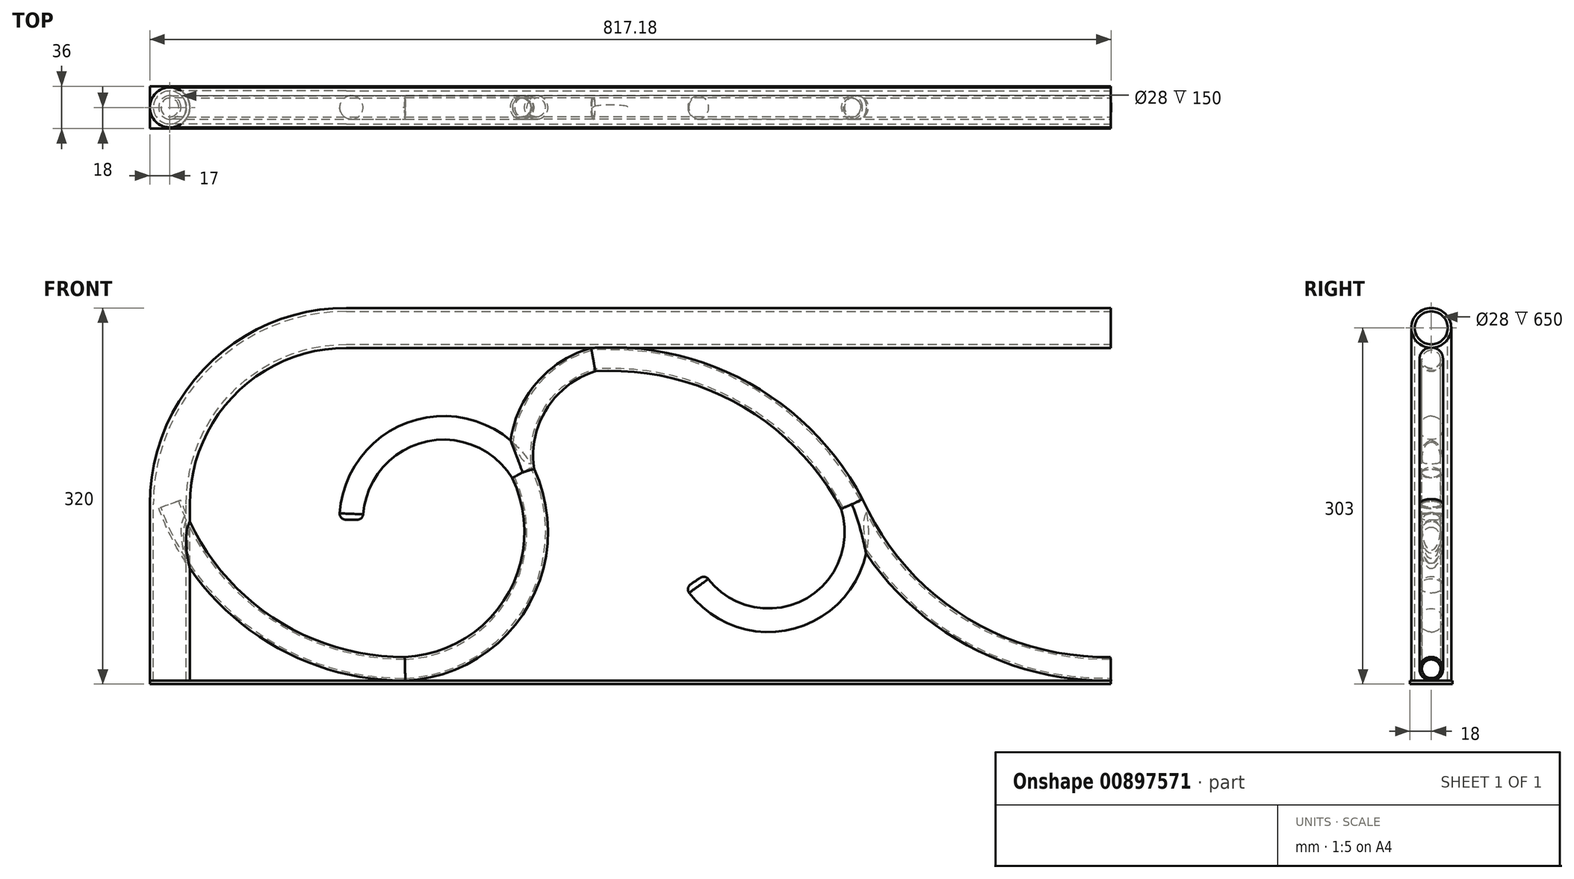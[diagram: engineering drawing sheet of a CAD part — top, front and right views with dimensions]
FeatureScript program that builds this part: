
annotation { "Feature Type Name" : "Feature", "Feature Type Description" : "" }
export const myFeature = defineFeature(function(context is Context, id is Id, definition is map)
    precondition{}
    {
        {
            var Q0;
            Q0=qCreatedBy(makeId("Front.planeOp"),FACE);
            var sketch = newSketch(context, id + "F0", { "sketchPlane" : qUnion([Q0])});
            skLineSegment(sketch, "E0", {"start": v(-800, 150) * mm, "end": v(-800, 0) * mm});
            skLineSegment(sketch, "E1", {"start": v(-800, 0) * mm, "end": v(0, 0) * mm});
            skLineSegment(sketch, "E2", {"start": v(0, 0) * mm, "end": v(0, 300) * mm});
            skLineSegment(sketch, "E3", {"start": v(-650, 300) * mm, "end": v(0, 300) * mm});
            skArc(sketch, "E4", {"start": v(-800, 150) * mm, "mid": v(-722.2, 48.28) * mm, "end": v(-600, 10) * mm});
            skLineSegment(sketch, "E5", {"start": v(-600, 10) * mm, "end": v(-600, 300) * mm, "construction": true});
            skLineSegment(sketch, "E6", {"start": v(-600, 177.08) * mm, "end": v(-500, 177.08) * mm, "construction": true});
            skArc(sketch, "E7", {"start": v(-600, 10) * mm, "mid": v(-505.06, 66.64) * mm, "end": v(-500, 177.08) * mm});
            skArc(sketch, "E8", {"start": v(-440, 273) * mm, "mid": v(-488.19, 236.41) * mm, "end": v(-500, 177.08) * mm});
            skLineSegment(sketch, "E9", {"start": v(0, 150) * mm, "end": v(-220, 150) * mm, "construction": true});
            skArc(sketch, "E10", {"start": v(-220, 150) * mm, "mid": v(-311.84, 244) * mm, "end": v(-440, 273) * mm});
            skArc(sketch, "E11", {"start": v(-220, 150) * mm, "mid": v(-131.05, 46.93) * mm, "end": v(0, 10.04) * mm});
            skArc(sketch, "E12", {"start": v(-353.24, 84.59) * mm, "mid": v(-258, 59.01) * mm, "end": v(-220, 150) * mm});
            skArc(sketch, "E13", {"start": v(-500, 177.08) * mm, "mid": v(-588.11, 212.15) * mm, "end": v(-645.78, 136.86) * mm});
            skPoint(sketch, "E14.visualSharp", {"position": v(-800, 300) * mm});
            skArc(sketch, "E14.filletArc", {"start": v(-650, 300) * mm, "mid": v(-756.07, 256.07) * mm, "end": v(-800, 150) * mm});
            skSolve(sketch);
        }
        {
            var Q0;
            Q0=sQuery(id+"F0.wireOp",EDGE,"E3");
            cPlane(context, id + "F1", {"entities" : qUnion([Q0]), "cplaneType" : CPlaneType.MID_PLANE, "offset" : 25 * mm, "width" : 150 * mm, "height" : 150 * mm});
        }
        {
            var Q0;
            Q0=qCreatedBy(id+"F1.planeOp",FACE);
            var sketch = newSketch(context, id + "F2", { "sketchPlane" : qUnion([Q0])});
            skCircle(sketch, "E15", {"center": v(0, 300) * mm, "radius": 17 * mm});
            skCircle(sketch, "E16", {"center": v(0, 300) * mm, "radius": 14 * mm});
            skSolve(sketch);
        }
        {
            var Q0;
            Q0=makeQuery(id+"F2.imprint","IMPRINT",FACE,{"disambiguationData":[TD([[makeQuery(id+"F2.imprint","IMPRINT",EDGE,{"derivedFrom":sQuery(id+"F2.wireOp",EDGE,"E15")}),1.0]])]});
            var Q1;
            Q1=sQuery(id+"F0.wireOp",EDGE,"E3");
            var Q2;
            Q2=sQuery(id+"F0.wireOp",EDGE,"E14.filletArc");
            var Q3;
            Q3=sQuery(id+"F0.wireOp",EDGE,"E0");
            sweep(context, id + "F3", {"profiles" : qUnion([Q0]), "path" : qUnion([Q1, Q2, Q3])});
        }
        {
            var Q0;
            Q0=sQuery(id+"F0.wireOp",EDGE,"E10");
            cPlane(context, id + "F4", {"entities" : qUnion([Q0]), "cplaneType" : CPlaneType.MID_PLANE, "offset" : 25 * mm, "width" : 150 * mm, "height" : 150 * mm});
        }
        {
            var Q0;
            Q0=qCreatedBy(id+"F4.planeOp",FACE);
            var sketch = newSketch(context, id + "F5", { "sketchPlane" : qUnion([Q0])});
            skCircle(sketch, "E17", {"center": v(0, 60.8) * mm, "radius": 10 * mm});
            skCircle(sketch, "E18", {"center": v(0, 60.8) * mm, "radius": 8 * mm});
            skSolve(sketch);
        }
        {
            var Q0;
            Q0=makeQuery(id+"F5.imprint","IMPRINT",FACE,{"disambiguationData":[TD([[makeQuery(id+"F5.imprint","IMPRINT",EDGE,{"derivedFrom":sQuery(id+"F5.wireOp",EDGE,"E17")}),1.0]])]});
            var Q1;
            Q1=sQuery(id+"F0.wireOp",EDGE,"E10");
            var Q2;
            Q2=sQuery(id+"F0.wireOp",EDGE,"E8");
            var Q3;
            Q3=sQuery(id+"F0.wireOp",EDGE,"E7");
            var Q4;
            Q4=sQuery(id+"F0.wireOp",EDGE,"E4");
            var Q5;
            Q5=sQuery(id+"F0.wireOp",EDGE,"E11");
            sweep(context, id + "F6", {"operationType" : NewBodyOperationType.ADD, "profiles" : qUnion([Q0]), "path" : qUnion([Q1, Q2, Q3, Q4, Q5])});
        }
        {
            var Q0;
            Q0=sQuery(id+"F0.wireOp",EDGE,"E13");
            cPlane(context, id + "F7", {"entities" : qUnion([Q0]), "cplaneType" : CPlaneType.MID_PLANE, "offset" : 25 * mm, "width" : 150 * mm, "height" : 150 * mm});
        }
        {
            var Q0;
            Q0=qCreatedBy(id+"F7.planeOp",FACE);
            var sketch = newSketch(context, id + "F8", { "sketchPlane" : qUnion([Q0])});
            skCircle(sketch, "E19", {"center": v(0, 360.9) * mm, "radius": 10 * mm});
            skSolve(sketch);
        }
        {
            var Q0;
            Q0=makeQuery(id+"F8.imprint","IMPRINT",FACE,{"disambiguationData":[TD([[makeQuery(id+"F8.imprint","IMPRINT",EDGE,{"derivedFrom":sQuery(id+"F8.wireOp",EDGE,"E19")}),1.0]])]});
            var Q1;
            Q1=sQuery(id+"F0.wireOp",EDGE,"E13");
            sweep(context, id + "F9", {"operationType" : NewBodyOperationType.ADD, "profiles" : qUnion([Q0]), "path" : qUnion([Q1])});
        }
        {
            var Q0;
            Q0=sQuery(id+"F0.wireOp",EDGE,"E12");
            cPlane(context, id + "F10", {"entities" : qUnion([Q0]), "cplaneType" : CPlaneType.MID_PLANE, "offset" : 25 * mm, "width" : 150 * mm, "height" : 150 * mm});
        }
        {
            var Q0;
            Q0=qCreatedBy(id+"F10.planeOp",FACE);
            var sketch = newSketch(context, id + "F11", { "sketchPlane" : qUnion([Q0])});
            skCircle(sketch, "E20", {"center": v(0, 166.67) * mm, "radius": 10 * mm});
            skSolve(sketch);
        }
        {
            var Q0;
            Q0=makeQuery(id+"F11.imprint","IMPRINT",FACE,{"disambiguationData":[TD([[makeQuery(id+"F11.imprint","IMPRINT",EDGE,{"derivedFrom":sQuery(id+"F11.wireOp",EDGE,"E20")}),1.0]])]});
            var Q1;
            Q1=sQuery(id+"F0.wireOp",EDGE,"E12");
            sweep(context, id + "F12", {"operationType" : NewBodyOperationType.ADD, "profiles" : qUnion([Q0]), "path" : qUnion([Q1])});
        }
        {
            var Q0;
            Q0=makeQuery(id+"F12.opSweep","CAP_EDGE",EDGE,{"disambiguationData":[OSD([sQuery(id+"F0.wireOp",VERTEX,"E12.start"),sQuery(id+"F11.wireOp",EDGE,"E20")])],"isStart":true});
            var Q1;
            Q1=makeQuery(id+"F9.opSweep","CAP_EDGE",EDGE,{"disambiguationData":[OSD([sQuery(id+"F0.wireOp",VERTEX,"E13.end"),sQuery(id+"F8.wireOp",EDGE,"E19")])],"isStart":false});
            fillet(context, id + "F13", {"entities" : qUnion([Q0, Q1]), "radius" : 5 * mm, "tangentPropagation" : true, "allowEdgeOverflow" : false});
        }
        {
            var Q0;
            Q0=sQuery(id+"F0.wireOp",EDGE,"E1");
            cPlane(context, id + "F14", {"entities" : qUnion([Q0]), "cplaneType" : CPlaneType.LINE_ANGLE, "offset" : 25 * mm, "angle" : 90 * degree, "width" : 150 * mm, "height" : 150 * mm});
        }
        {
            var Q0;
            Q0=qCreatedBy(id+"F14.planeOp",FACE);
            var sketch = newSketch(context, id + "F15", { "sketchPlane" : qUnion([Q0])});
            skLineSegment(sketch, "E21.bottom", {"start": v(0, -18) * mm, "end": v(-817, -18) * mm});
            skLineSegment(sketch, "E21.top", {"start": v(0, 18) * mm, "end": v(-817, 18) * mm});
            skLineSegment(sketch, "E21.right", {"start": v(-817, -18) * mm, "end": v(-817, 18) * mm});
            skPoint(sketch, "E21.middle", {"position": v(-400, 0) * mm});
            skLineSegment(sketch, "E22", {"start": v(-800, 18) * mm, "end": v(-800, -18) * mm, "construction": true});
            skLineSegment(sketch, "E23", {"start": v(0, -18) * mm, "end": v(0, 18) * mm});
            skPoint(sketch, "E21.left.start.orphan", {"position": v(17, -18) * mm});
            skPoint(sketch, "E24.orphan", {"position": v(17, 18) * mm});
            skSolve(sketch);
        }
        {
            var Q0;
            Q0 = qSketchRegion(id + "F15", true);
            extrude(context, id + "F16", {"entities" : qUnion([Q0]), "operationType" : NewBodyOperationType.ADD, "oppositeDirection" : true, "depth" : 3 * mm, "offsetDistance" : 25 * mm});
        }
    });
